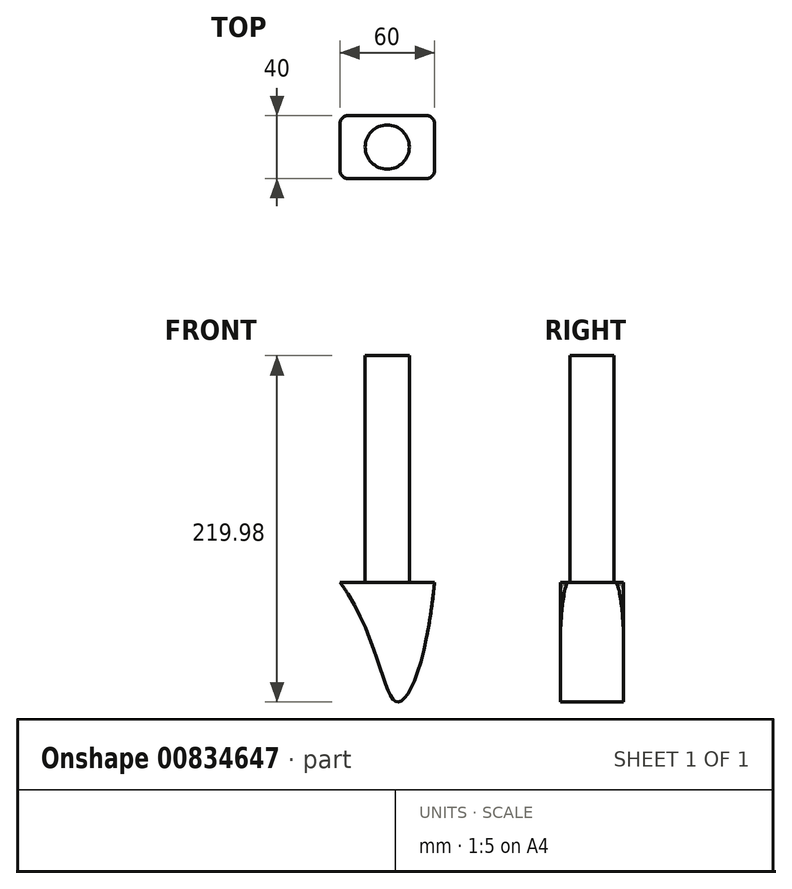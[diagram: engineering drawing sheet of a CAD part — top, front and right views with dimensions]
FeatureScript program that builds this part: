
annotation { "Feature Type Name" : "Feature", "Feature Type Description" : "" }
export const myFeature = defineFeature(function(context is Context, id is Id, definition is map)
    precondition{}
    {
        {
            var Q0;
            Q0=qCreatedBy(makeId("Top.planeOp"),FACE);
            var sketch = newSketch(context, id + "F0", { "sketchPlane" : qUnion([Q0])});
            skCircle(sketch, "E0", {"center": v(0, 0) * mm, "radius": 14 * mm});
            skSolve(sketch);
        }
        {
            var Q0;
            Q0 = qSketchRegion(id + "F0", true);
            var Q1;
            Q1=makeQuery(id+"F0.imprint","IMPRINT",FACE,{"disambiguationData":[TD([[makeQuery(id+"F0.imprint","IMPRINT",EDGE,{"derivedFrom":sQuery(id+"F0.wireOp",EDGE,"E0")}),1.0]])]});
            extrude(context, id + "F1", {"entities" : qUnion([Q0, Q1]), "depth" : 144 * mm, "offsetDistance" : 25 * mm});
        }
        {
            var Q0;
            Q0=qCreatedBy(makeId("Top.planeOp"),FACE);
            var sketch = newSketch(context, id + "F2", { "sketchPlane" : qUnion([Q0])});
            skLineSegment(sketch, "E1.bottom", {"start": v(30, 20) * mm, "end": v(-30, 20) * mm});
            skLineSegment(sketch, "E1.top", {"start": v(30, -20) * mm, "end": v(-30, -20) * mm});
            skLineSegment(sketch, "E1.left", {"start": v(30, 20) * mm, "end": v(30, -20) * mm});
            skLineSegment(sketch, "E1.right", {"start": v(-30, 20) * mm, "end": v(-30, -20) * mm});
            skPoint(sketch, "E1.middle", {"position": v(0, 0) * mm});
            skSolve(sketch);
        }
        {
            var Q0;
            Q0 = qSketchRegion(id + "F2", true);
            var Q1;
            Q1=makeQuery(id+"F2.imprint","IMPRINT",FACE,{"disambiguationData":[TD([[makeQuery(id+"F2.imprint","IMPRINT",EDGE,{"derivedFrom":sQuery(id+"F2.wireOp",EDGE,"E1.bottom")}),1.0]])]});
            extrude(context, id + "F3", {"entities" : qUnion([Q0, Q1]), "operationType" : NewBodyOperationType.ADD, "oppositeDirection" : true, "depth" : 80 * mm, "offsetDistance" : 25 * mm});
        }
        {
            var Q0;
            Q0=makeQuery(id+"F3.opExtrude","SWEPT_EDGE",EDGE,{"disambiguationData":[OSD([sQuery(id+"F2.wireOp",EDGE,"E1.top"),sQuery(id+"F2.wireOp",EDGE,"E1.right")])]});
            var Q1;
            Q1=makeQuery(id+"F3.opExtrude","SWEPT_EDGE",EDGE,{"disambiguationData":[OSD([sQuery(id+"F2.wireOp",EDGE,"E1.bottom"),sQuery(id+"F2.wireOp",EDGE,"E1.right")])]});
            var Q2;
            Q2=makeQuery(id+"F3.opExtrude","SWEPT_EDGE",EDGE,{"disambiguationData":[OSD([sQuery(id+"F2.wireOp",EDGE,"E1.top"),sQuery(id+"F2.wireOp",EDGE,"E1.left")])]});
            var Q3;
            Q3=makeQuery(id+"F3.opExtrude","SWEPT_EDGE",EDGE,{"disambiguationData":[OSD([sQuery(id+"F2.wireOp",EDGE,"E1.bottom"),sQuery(id+"F2.wireOp",EDGE,"E1.left")])]});
            fillet(context, id + "F4", {"entities" : qUnion([Q0, Q1, Q2, Q3]), "radius" : 5 * mm, "tangentPropagation" : true, "allowEdgeOverflow" : false});
        }
        {
            var Q0;
            Q0=makeQuery(id+"F3.opExtrude","SWEPT_FACE",FACE,{"disambiguationData":[OSD([sQuery(id+"F2.wireOp",EDGE,"E1.top")])]});
            var sketch = newSketch(context, id + "F5", { "sketchPlane" : qUnion([Q0])});
            skLineSegment(sketch, "E2.bottom", {"start": v(-30, 0) * mm, "end": v(30, 0) * mm});
            skLineSegment(sketch, "E2.top", {"start": v(-30, -90) * mm, "end": v(30, -90) * mm});
            skLineSegment(sketch, "E2.left", {"start": v(-30, 0) * mm, "end": v(-30, -90) * mm});
            skLineSegment(sketch, "E2.right", {"start": v(30, 0) * mm, "end": v(30, -90) * mm});
            skPoint(sketch, "E3.1.internal.snap0", {"position": v(5, -80) * mm});
            skFitSpline(sketch, "E3", {"points": [v(-30, 0) * mm, v(5, -75.5) * mm, v(30, 0) * mm], "startDerivative": vector(139.28, -189) * mm, "endDerivative": vector(30.34, 315.43) * mm});
            skSolve(sketch);
        }
        {
            var Q0;
            {var subQ1=sQuery(id+"F2.wireOp",EDGE,"E1.top");var subQ7=makeQuery(id+"F3.opExtrude","CAP_EDGE",EDGE,{"disambiguationData":[OSD([subQ1])],"isStart":false});Q0=makeQuery(id+"F5.imprint","IMPRINT",FACE,{"disambiguationData":[TD([[makeQuery(id+"F5.imprint","IMPRINT",EDGE,{"derivedFrom":subQ7}),-1.0]])]});}
            var Q1;
            Q1=makeQuery(id+"F5.imprint","IMPRINT",FACE,{"disambiguationData":[TD([[makeQuery(id+"F5.imprint","IMPRINT",EDGE,{"derivedFrom":sQuery(id+"F5.wireOp",EDGE,"E2.top")}),1.0]])]});
            extrude(context, id + "F6", {"entities" : qUnion([Q0, Q1]), "operationType" : NewBodyOperationType.REMOVE, "oppositeDirection" : true, "depth" : 80 * mm, "offsetDistance" : 25 * mm});
        }
    });
